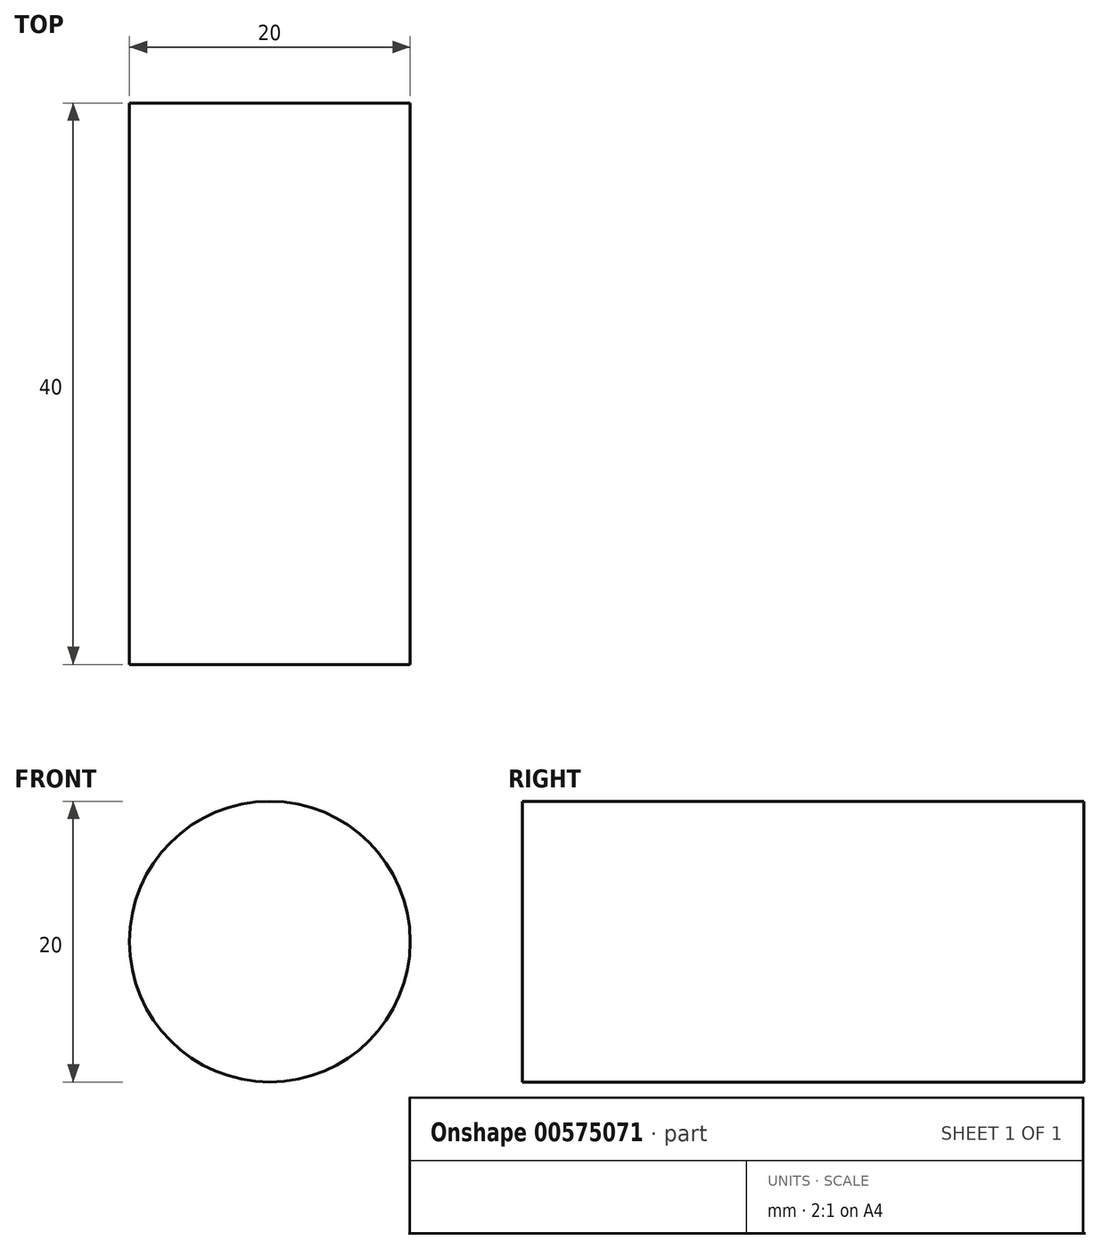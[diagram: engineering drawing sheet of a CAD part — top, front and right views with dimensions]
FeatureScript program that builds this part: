
annotation { "Feature Type Name" : "Feature", "Feature Type Description" : "" }
export const myFeature = defineFeature(function(context is Context, id is Id, definition is map)
    precondition{}
    {
        {
            var Q0;
            Q0=qCreatedBy(makeId("Front.planeOp"),FACE);
            var sketch = newSketch(context, id + "F0", { "sketchPlane" : qUnion([Q0])});
            skCircle(sketch, "E0", {"center": v(0, 0) * mm, "radius": 10 * mm});
            skSolve(sketch);
        }
        {
            var Q0;
            Q0=makeQuery(id+"F0.imprint","IMPRINT",FACE,{"disambiguationData":[TD([[makeQuery(id+"F0.imprint","IMPRINT",EDGE,{"derivedFrom":sQuery(id+"F0.wireOp",EDGE,"E0")}),1.0]])]});
            var Q1;
            Q1=sQuery(id+"F0.wireOp",EDGE,"E0");
            extrude(context, id + "F1", {"entities" : qUnion([Q0]), "surfaceEntities" : qUnion([Q1]), "depth" : 40 * mm, "offsetDistance" : 25 * mm, "symmetric" : true});
        }
    });
